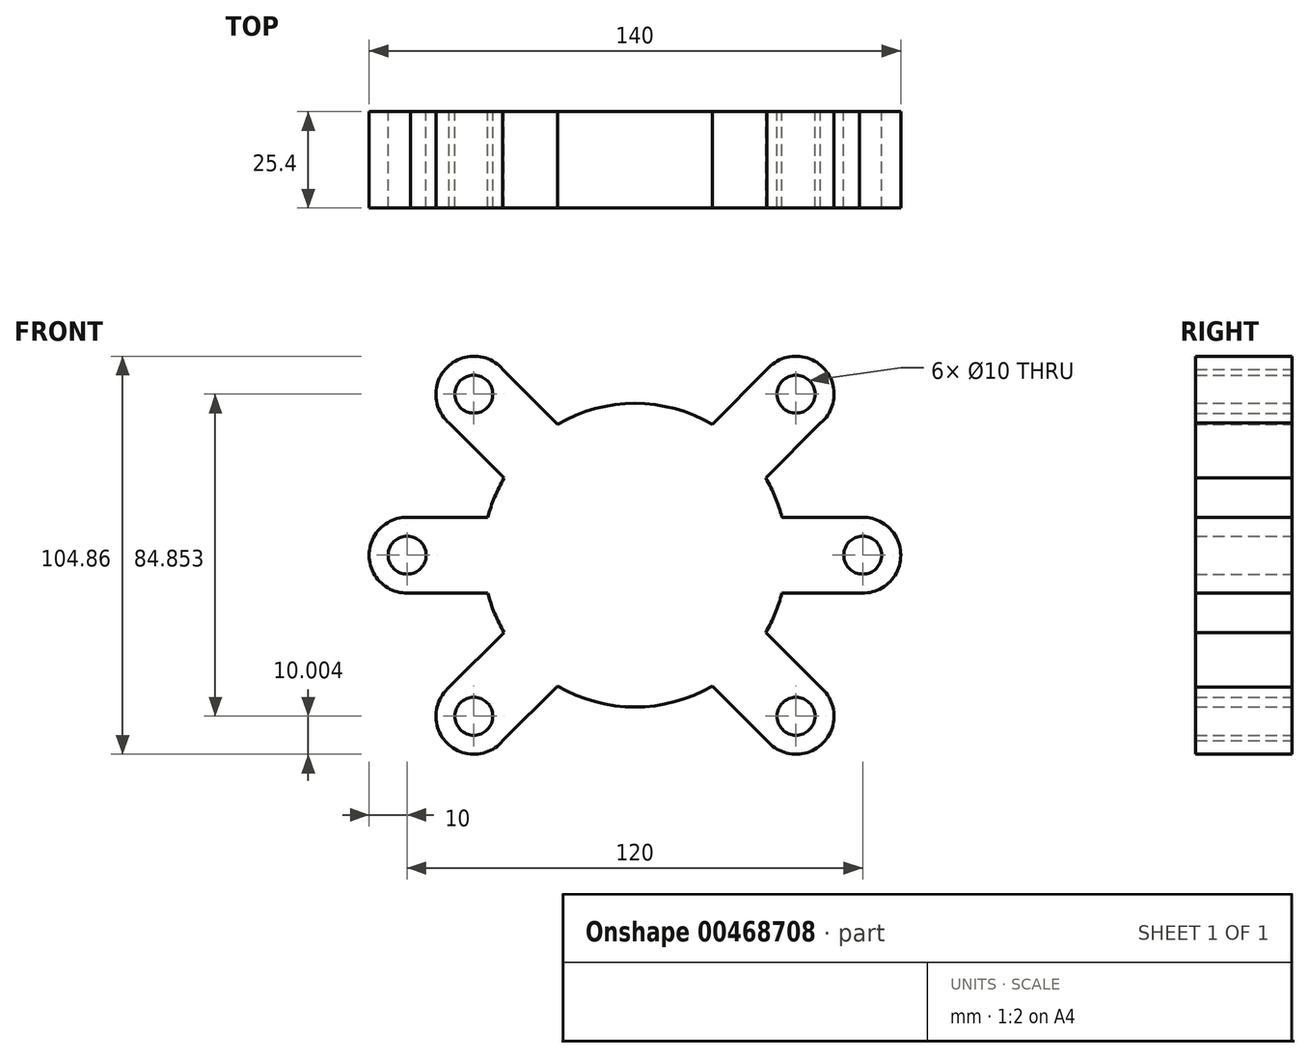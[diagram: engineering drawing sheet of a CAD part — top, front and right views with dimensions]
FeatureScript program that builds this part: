
annotation { "Feature Type Name" : "Feature", "Feature Type Description" : "" }
export const myFeature = defineFeature(function(context is Context, id is Id, definition is map)
    precondition{}
    {
        {
            var Q0;
            Q0=qCreatedBy(makeId("Front.planeOp"),FACE);
            var sketch = newSketch(context, id + "F0", { "sketchPlane" : qUnion([Q0])});
            skCircle(sketch, "E0", {"center": v(0, 0) * mm, "radius": 30 * mm});
            skArc(sketch, "E1", {"start": v(-34.44, 20.35) * mm, "mid": v(-36.96, 15.3) * mm, "end": v(-38.74, 9.97) * mm});
            skArc(sketch, "E2", {"start": v(-59.8, -5) * mm, "mid": v(-56.34, -20.63) * mm, "end": v(-48.88, -34.8) * mm, "construction": true});
            skLineSegment(sketch, "E3", {"start": v(-38.74, 9.97) * mm, "end": v(-59.17, 9.97) * mm});
            skLineSegment(sketch, "E4.MirrorCS", {"start": v(-38.74, -9.97) * mm, "end": v(-59.17, -9.97) * mm});
            skPoint(sketch, "E5", {"position": v(-60, 0) * mm});
            skCircle(sketch, "E6", {"center": v(-60, 0) * mm, "radius": 5 * mm});
            skArc(sketch, "E7", {"start": v(-59.17, 9.97) * mm, "mid": v(-70, 0) * mm, "end": v(-59.17, -9.97) * mm});
            skLineSegment(sketch, "E8.1.0", {"start": v(-34.44, -20.35) * mm, "end": v(-48.88, -34.8) * mm});
            skLineSegment(sketch, "E8.1.1", {"start": v(-20.35, -34.44) * mm, "end": v(-34.8, -48.88) * mm});
            skArc(sketch, "E8.1.2", {"start": v(-48.88, -34.8) * mm, "mid": v(-49.5, -49.5) * mm, "end": v(-34.8, -48.88) * mm});
            skLineSegment(sketch, "E8.3.0", {"start": v(20.35, -34.44) * mm, "end": v(34.8, -48.88) * mm});
            skLineSegment(sketch, "E8.3.1", {"start": v(34.44, -20.35) * mm, "end": v(48.88, -34.8) * mm});
            skArc(sketch, "E8.3.2", {"start": v(34.8, -48.88) * mm, "mid": v(49.5, -49.5) * mm, "end": v(48.88, -34.8) * mm});
            skLineSegment(sketch, "E8.4.0", {"start": v(38.74, -9.97) * mm, "end": v(59.17, -9.97) * mm});
            skLineSegment(sketch, "E8.4.1", {"start": v(38.74, 9.97) * mm, "end": v(59.17, 9.97) * mm});
            skArc(sketch, "E8.4.2", {"start": v(59.17, -9.97) * mm, "mid": v(70, 0) * mm, "end": v(59.17, 9.97) * mm});
            skLineSegment(sketch, "E8.5.0", {"start": v(34.44, 20.35) * mm, "end": v(48.88, 34.8) * mm});
            skLineSegment(sketch, "E8.5.1", {"start": v(20.35, 34.44) * mm, "end": v(34.8, 48.88) * mm});
            skArc(sketch, "E8.5.2", {"start": v(48.88, 34.8) * mm, "mid": v(49.5, 49.5) * mm, "end": v(34.8, 48.88) * mm});
            skLineSegment(sketch, "E8.7.0", {"start": v(-20.35, 34.44) * mm, "end": v(-34.8, 48.88) * mm});
            skLineSegment(sketch, "E8.7.1", {"start": v(-34.44, 20.35) * mm, "end": v(-48.88, 34.8) * mm});
            skArc(sketch, "E8.7.2", {"start": v(-34.8, 48.88) * mm, "mid": v(-49.5, 49.5) * mm, "end": v(-48.88, 34.8) * mm});
            skCircle(sketch, "E9.1.0", {"center": v(-42.43, -42.43) * mm, "radius": 5 * mm});
            skCircle(sketch, "E9.3.0", {"center": v(42.43, -42.43) * mm, "radius": 5 * mm});
            skCircle(sketch, "E9.4.0", {"center": v(60, 0) * mm, "radius": 5 * mm});
            skCircle(sketch, "E9.5.0", {"center": v(42.43, 42.43) * mm, "radius": 5 * mm});
            skCircle(sketch, "E9.7.0", {"center": v(-42.43, 42.43) * mm, "radius": 5 * mm});
            skArc(sketch, "E10.trimOffspring", {"start": v(20.35, 34.44) * mm, "mid": v(0, 40) * mm, "end": v(-20.35, 34.44) * mm});
            skArc(sketch, "E11.trimOffspring", {"start": v(-38.74, -9.97) * mm, "mid": v(-36.96, -15.3) * mm, "end": v(-34.44, -20.35) * mm});
            skArc(sketch, "E12.trimOffspring", {"start": v(-20.35, -34.44) * mm, "mid": v(0, -40) * mm, "end": v(20.35, -34.44) * mm});
            skArc(sketch, "E13.trimOffspring", {"start": v(34.44, -20.35) * mm, "mid": v(36.96, -15.3) * mm, "end": v(38.74, -9.97) * mm});
            skArc(sketch, "E14.trimOffspring", {"start": v(38.74, 9.97) * mm, "mid": v(36.96, 15.3) * mm, "end": v(34.44, 20.35) * mm});
            skArc(sketch, "E15.trimOffspring", {"start": v(-48.88, 34.8) * mm, "mid": v(-56.34, 20.63) * mm, "end": v(-59.8, 5) * mm, "construction": true});
            skSolve(sketch);
        }
        {
            var Q0;
            Q0=makeQuery(id+"F0.imprint","IMPRINT",FACE,{"disambiguationData":[TD([[makeQuery(id+"F0.imprint","IMPRINT",EDGE,{"derivedFrom":sQuery(id+"F0.wireOp",EDGE,"E0")}),1.0]])]});
            var Q1;
            Q1=makeQuery(id+"F0.imprint","IMPRINT",FACE,{"disambiguationData":[TD([[makeQuery(id+"F0.imprint","IMPRINT",EDGE,{"derivedFrom":sQuery(id+"F0.wireOp",EDGE,"E0")}),-1.0]])]});
            extrude(context, id + "F1", {"entities" : qUnion([Q0, Q1]), "endBound" : BoundingType.SYMMETRIC, "depth" : 25.4 * mm});
        }
    });
